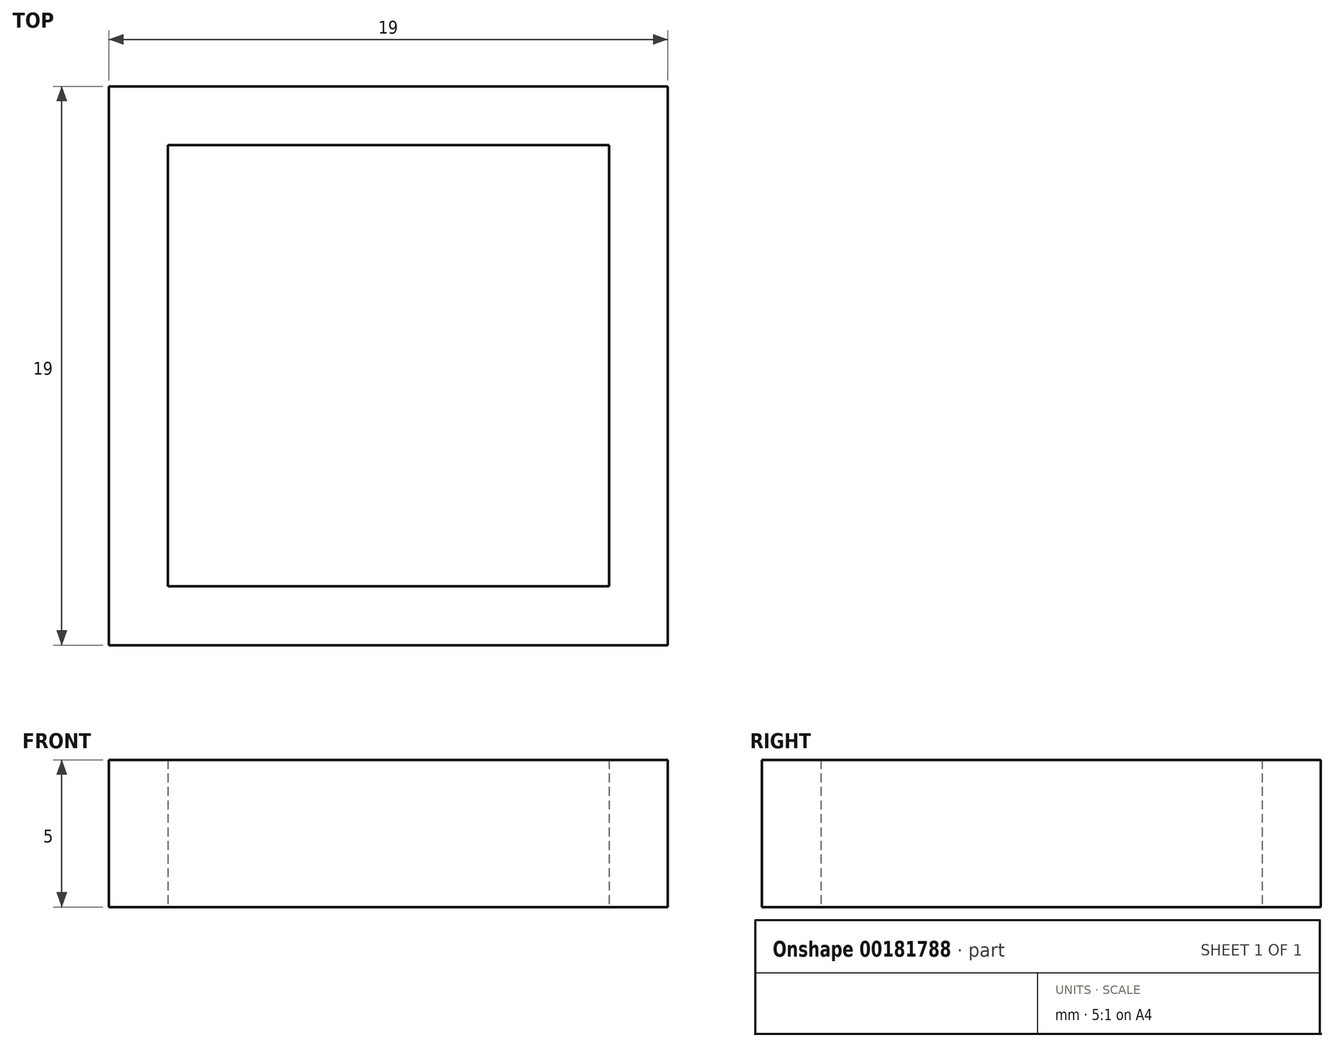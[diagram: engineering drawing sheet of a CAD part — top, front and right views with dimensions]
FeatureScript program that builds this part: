
annotation { "Feature Type Name" : "Feature", "Feature Type Description" : "" }
export const myFeature = defineFeature(function(context is Context, id is Id, definition is map)
    precondition{}
    {
        {
            var Q0;
            Q0=qCreatedBy(makeId("Top.planeOp"),FACE);
            var sketch = newSketch(context, id + "F0", { "sketchPlane" : qUnion([Q0])});
            skLineSegment(sketch, "E0.bottom", {"start": v(7.5, -7.5) * mm, "end": v(-7.5, -7.5) * mm});
            skLineSegment(sketch, "E0.top", {"start": v(7.5, 7.5) * mm, "end": v(-7.5, 7.5) * mm});
            skLineSegment(sketch, "E0.left", {"start": v(7.5, -7.5) * mm, "end": v(7.5, 7.5) * mm});
            skLineSegment(sketch, "E0.right", {"start": v(-7.5, -7.5) * mm, "end": v(-7.5, 7.5) * mm});
            skPoint(sketch, "E0.middle", {"position": v(0, 0) * mm});
            skLineSegment(sketch, "E1.0", {"start": v(-9.5, -9.5) * mm, "end": v(-9.5, 9.5) * mm});
            skLineSegment(sketch, "E1.1", {"start": v(9.5, -9.5) * mm, "end": v(-9.5, -9.5) * mm});
            skLineSegment(sketch, "E1.2", {"start": v(9.5, -9.5) * mm, "end": v(9.5, 9.5) * mm});
            skLineSegment(sketch, "E1.3", {"start": v(9.5, 9.5) * mm, "end": v(-9.5, 9.5) * mm});
            skSolve(sketch);
        }
        {
            var Q0;
            Q0 = qSketchRegion(id + "F0", true);
            extrude(context, id + "F1", {"entities" : qUnion([Q0]), "depth" : 5 * mm});
        }
    });
